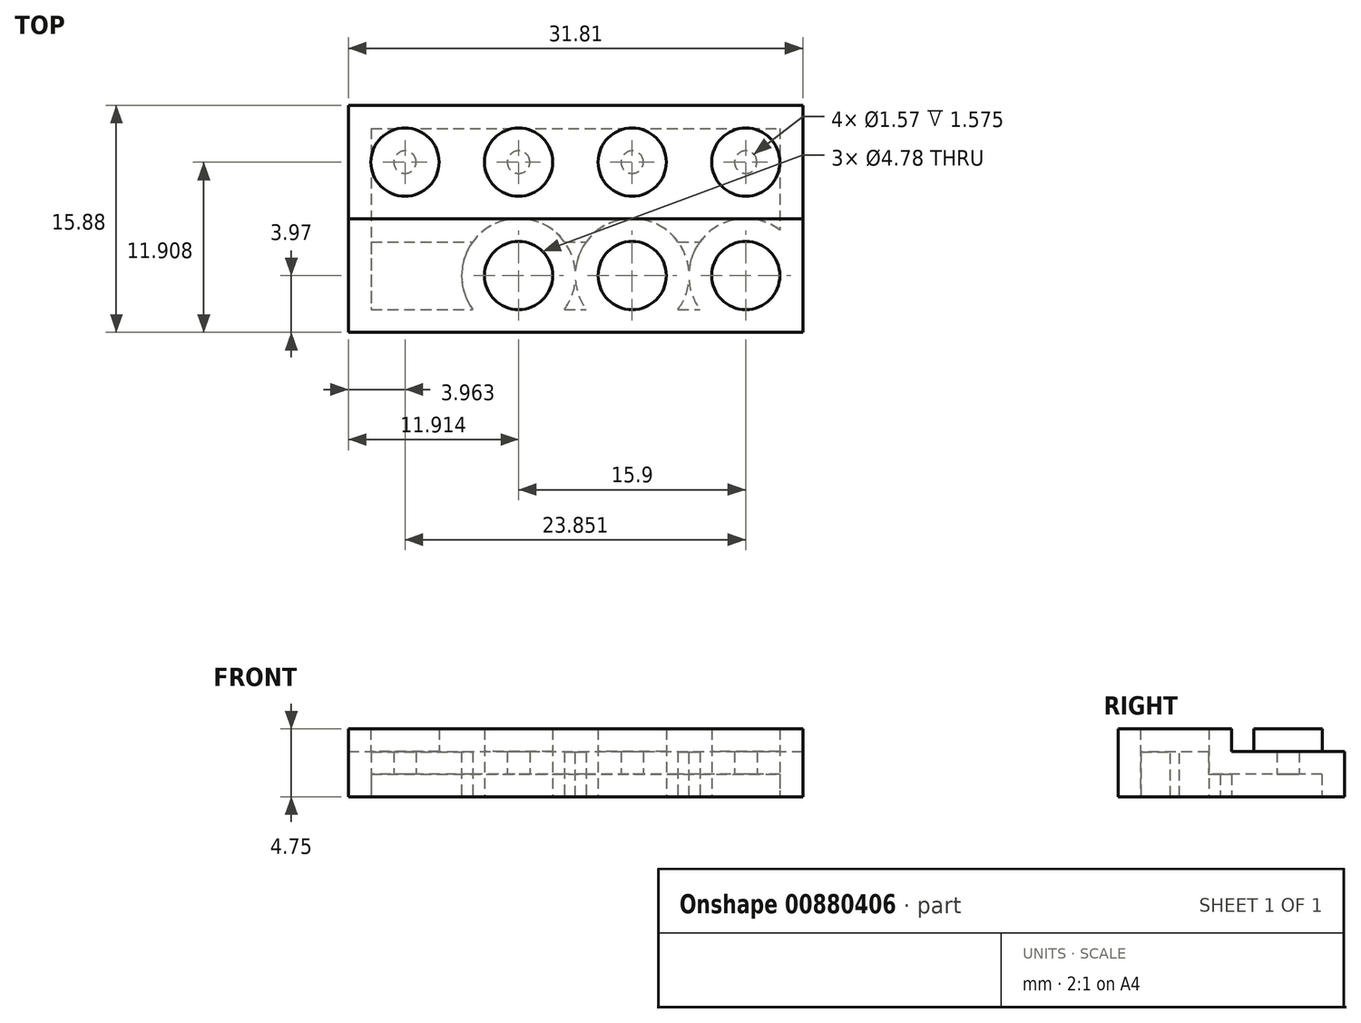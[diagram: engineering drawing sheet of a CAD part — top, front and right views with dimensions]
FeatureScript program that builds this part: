
annotation { "Feature Type Name" : "Feature", "Feature Type Description" : "" }
export const myFeature = defineFeature(function(context is Context, id is Id, definition is map)
    precondition{}
    {
        {
            var Q0;
            Q0=qCreatedBy(makeId("Top.planeOp"),FACE);
            var sketch = newSketch(context, id + "F0", { "sketchPlane" : qUnion([Q0])});
            skLineSegment(sketch, "E0.bottom", {"start": v(-38.8, 8.6) * mm, "end": v(-7, 8.6) * mm});
            skLineSegment(sketch, "E0.top", {"start": v(-38.8, -7.28) * mm, "end": v(-7, -7.28) * mm});
            skLineSegment(sketch, "E0.left", {"start": v(-38.8, 8.6) * mm, "end": v(-38.8, -7.28) * mm});
            skLineSegment(sketch, "E0.right", {"start": v(-7, 8.6) * mm, "end": v(-7, -7.28) * mm});
            skLineSegment(sketch, "E1", {"start": v(-38.8, 0.66) * mm, "end": v(-7, 0.66) * mm});
            skLineSegment(sketch, "E2", {"start": v(-7, 8.6) * mm, "end": v(-7, 0.66) * mm});
            skLineSegment(sketch, "E3", {"start": v(-7, 0.66) * mm, "end": v(-7, -7.28) * mm});
            skLineSegment(sketch, "E4", {"start": v(-38.8, 8.6) * mm, "end": v(-38.8, 0.66) * mm});
            skLineSegment(sketch, "E5", {"start": v(-38.8, -7.28) * mm, "end": v(-38.8, 0.66) * mm});
            skLineSegment(sketch, "E6", {"start": v(-7, -3.31) * mm, "end": v(-38.8, -3.31) * mm});
            skLineSegment(sketch, "E7", {"start": v(-38.8, -3.31) * mm, "end": v(-38.8, 4.63) * mm});
            skLineSegment(sketch, "E8", {"start": v(-38.8, 4.63) * mm, "end": v(-7, 4.63) * mm});
            skCircle(sketch, "E9", {"center": v(-34.85, 4.63) * mm, "radius": 2.39 * mm});
            skCircle(sketch, "E10.1.0.0", {"center": v(-26.9, 4.63) * mm, "radius": 2.39 * mm});
            skCircle(sketch, "E10.2.0.0", {"center": v(-18.95, 4.63) * mm, "radius": 2.39 * mm});
            skCircle(sketch, "E10.3.0.0", {"center": v(-11, 4.63) * mm, "radius": 2.39 * mm});
            skLineSegment(sketch, "E10.direction1", {"start": v(-34.85, 4.63) * mm, "end": v(-26.9, 4.63) * mm, "construction": true});
            skCircle(sketch, "E11.MirrorC", {"center": v(-34.85, -3.31) * mm, "radius": 2.39 * mm});
            skCircle(sketch, "E12.MirrorC", {"center": v(-26.9, -3.31) * mm, "radius": 2.39 * mm});
            skCircle(sketch, "E13.MirrorC", {"center": v(-18.95, -3.31) * mm, "radius": 2.39 * mm});
            skCircle(sketch, "E14.MirrorC", {"center": v(-11, -3.31) * mm, "radius": 2.39 * mm});
            skSolve(sketch);
        }
        {
            var Q0;
            {var subQ8=sQuery(id+"F0.wireOp",EDGE,"E0.bottom");Q0=makeQuery(id+"F0.imprint","IMPRINT",FACE,{"disambiguationData":[TD([[makeQuery(id+"F0.imprint","IMPRINT",EDGE,{"derivedFrom":subQ8}),-1.0]])]});}
            var Q1;
            {var subQ12=sQuery(id+"F0.wireOp",EDGE,"E1");Q1=makeQuery(id+"F0.imprint","IMPRINT",FACE,{"disambiguationData":[TD([[makeQuery(id+"F0.imprint","IMPRINT",EDGE,{"derivedFrom":subQ12}),1.0]])]});}
            var Q2;
            {var subQ12=sQuery(id+"F0.wireOp",EDGE,"E0.top");Q2=makeQuery(id+"F0.imprint","IMPRINT",FACE,{"disambiguationData":[TD([[makeQuery(id+"F0.imprint","IMPRINT",EDGE,{"derivedFrom":subQ12}),1.0]])]});}
            var Q3;
            {var subQ8=sQuery(id+"F0.wireOp",EDGE,"E1");Q3=makeQuery(id+"F0.imprint","IMPRINT",FACE,{"disambiguationData":[TD([[makeQuery(id+"F0.imprint","IMPRINT",EDGE,{"derivedFrom":subQ8}),-1.0]])]});}
            extrude(context, id + "F1", {"entities" : qUnion([Q0, Q1, Q2, Q3]), "depth" : 3.17 * mm, "offsetDistance" : 25.4 * mm});
        }
        {
            var Q0;
            {var subQ0=sQuery(id+"F0.wireOp",EDGE,"E9");var subQ1=sQuery(id+"F0.wireOp",EDGE,"E8");var subQ2=makeQuery(id+"F0.imprint","INTERSECT",VERTEX,{"disambiguationData":[OD(0.0)],"derivedFrom":[subQ1,subQ0]});Q0=makeQuery(id+"F0.imprint","IMPRINT",FACE,{"disambiguationData":[TD([[makeQuery(id+"F0.imprint","IMPRINT",EDGE,{"disambiguationData":[TD([[subQ2,-1.0]])],"derivedFrom":subQ1}),-1.0]])]});}
            var Q1;
            {var subQ0=sQuery(id+"F0.wireOp",EDGE,"E9");var subQ1=sQuery(id+"F0.wireOp",EDGE,"E8");var subQ2=makeQuery(id+"F0.imprint","INTERSECT",VERTEX,{"disambiguationData":[OD(0.0)],"derivedFrom":[subQ1,subQ0]});Q1=makeQuery(id+"F0.imprint","IMPRINT",FACE,{"disambiguationData":[TD([[makeQuery(id+"F0.imprint","IMPRINT",EDGE,{"disambiguationData":[TD([[subQ2,-1.0]])],"derivedFrom":subQ1}),1.0]])]});}
            var Q2;
            {var subQ0=sQuery(id+"F0.wireOp",EDGE,"E11.MirrorC");var subQ1=sQuery(id+"F0.wireOp",EDGE,"E6");var subQ2=makeQuery(id+"F0.imprint","INTERSECT",VERTEX,{"disambiguationData":[OD(0.0)],"derivedFrom":[subQ1,subQ0]});Q2=makeQuery(id+"F0.imprint","IMPRINT",FACE,{"disambiguationData":[TD([[makeQuery(id+"F0.imprint","IMPRINT",EDGE,{"disambiguationData":[TD([[subQ2,-1.0]])],"derivedFrom":subQ1}),-1.0]])]});}
            var Q3;
            {var subQ0=sQuery(id+"F0.wireOp",EDGE,"E11.MirrorC");var subQ1=sQuery(id+"F0.wireOp",EDGE,"E6");var subQ2=makeQuery(id+"F0.imprint","INTERSECT",VERTEX,{"disambiguationData":[OD(0.0)],"derivedFrom":[subQ1,subQ0]});Q3=makeQuery(id+"F0.imprint","IMPRINT",FACE,{"disambiguationData":[TD([[makeQuery(id+"F0.imprint","IMPRINT",EDGE,{"disambiguationData":[TD([[subQ2,-1.0]])],"derivedFrom":subQ1}),1.0]])]});}
            var Q4;
            {var subQ0=sQuery(id+"F0.wireOp",EDGE,"E12.MirrorC");var subQ1=sQuery(id+"F0.wireOp",EDGE,"E6");var subQ2=makeQuery(id+"F0.imprint","INTERSECT",VERTEX,{"disambiguationData":[OD(0.0)],"derivedFrom":[subQ1,subQ0]});Q4=makeQuery(id+"F0.imprint","IMPRINT",FACE,{"disambiguationData":[TD([[makeQuery(id+"F0.imprint","IMPRINT",EDGE,{"disambiguationData":[TD([[subQ2,-1.0]])],"derivedFrom":subQ1}),1.0]])]});}
            var Q5;
            {var subQ0=sQuery(id+"F0.wireOp",EDGE,"E12.MirrorC");var subQ1=sQuery(id+"F0.wireOp",EDGE,"E6");var subQ2=makeQuery(id+"F0.imprint","INTERSECT",VERTEX,{"disambiguationData":[OD(0.0)],"derivedFrom":[subQ1,subQ0]});Q5=makeQuery(id+"F0.imprint","IMPRINT",FACE,{"disambiguationData":[TD([[makeQuery(id+"F0.imprint","IMPRINT",EDGE,{"disambiguationData":[TD([[subQ2,-1.0]])],"derivedFrom":subQ1}),-1.0]])]});}
            var Q6;
            {var subQ0=sQuery(id+"F0.wireOp",EDGE,"E10.1.0.0");var subQ1=sQuery(id+"F0.wireOp",EDGE,"E8");var subQ2=makeQuery(id+"F0.imprint","INTERSECT",VERTEX,{"disambiguationData":[OD(0.0)],"derivedFrom":[subQ1,subQ0]});Q6=makeQuery(id+"F0.imprint","IMPRINT",FACE,{"disambiguationData":[TD([[makeQuery(id+"F0.imprint","IMPRINT",EDGE,{"disambiguationData":[TD([[subQ2,-1.0]])],"derivedFrom":subQ1}),-1.0]])]});}
            var Q7;
            {var subQ0=sQuery(id+"F0.wireOp",EDGE,"E10.1.0.0");var subQ1=sQuery(id+"F0.wireOp",EDGE,"E8");var subQ2=makeQuery(id+"F0.imprint","INTERSECT",VERTEX,{"disambiguationData":[OD(0.0)],"derivedFrom":[subQ1,subQ0]});Q7=makeQuery(id+"F0.imprint","IMPRINT",FACE,{"disambiguationData":[TD([[makeQuery(id+"F0.imprint","IMPRINT",EDGE,{"disambiguationData":[TD([[subQ2,-1.0]])],"derivedFrom":subQ1}),1.0]])]});}
            var Q8;
            {var subQ0=sQuery(id+"F0.wireOp",EDGE,"E13.MirrorC");var subQ1=sQuery(id+"F0.wireOp",EDGE,"E6");var subQ2=makeQuery(id+"F0.imprint","INTERSECT",VERTEX,{"disambiguationData":[OD(0.0)],"derivedFrom":[subQ1,subQ0]});Q8=makeQuery(id+"F0.imprint","IMPRINT",FACE,{"disambiguationData":[TD([[makeQuery(id+"F0.imprint","IMPRINT",EDGE,{"disambiguationData":[TD([[subQ2,-1.0]])],"derivedFrom":subQ1}),1.0]])]});}
            var Q9;
            {var subQ0=sQuery(id+"F0.wireOp",EDGE,"E13.MirrorC");var subQ1=sQuery(id+"F0.wireOp",EDGE,"E6");var subQ2=makeQuery(id+"F0.imprint","INTERSECT",VERTEX,{"disambiguationData":[OD(0.0)],"derivedFrom":[subQ1,subQ0]});Q9=makeQuery(id+"F0.imprint","IMPRINT",FACE,{"disambiguationData":[TD([[makeQuery(id+"F0.imprint","IMPRINT",EDGE,{"disambiguationData":[TD([[subQ2,-1.0]])],"derivedFrom":subQ1}),-1.0]])]});}
            var Q10;
            {var subQ0=sQuery(id+"F0.wireOp",EDGE,"E10.2.0.0");var subQ1=sQuery(id+"F0.wireOp",EDGE,"E8");var subQ2=makeQuery(id+"F0.imprint","INTERSECT",VERTEX,{"disambiguationData":[OD(0.0)],"derivedFrom":[subQ1,subQ0]});Q10=makeQuery(id+"F0.imprint","IMPRINT",FACE,{"disambiguationData":[TD([[makeQuery(id+"F0.imprint","IMPRINT",EDGE,{"disambiguationData":[TD([[subQ2,-1.0]])],"derivedFrom":subQ1}),1.0]])]});}
            var Q11;
            {var subQ0=sQuery(id+"F0.wireOp",EDGE,"E10.2.0.0");var subQ1=sQuery(id+"F0.wireOp",EDGE,"E8");var subQ2=makeQuery(id+"F0.imprint","INTERSECT",VERTEX,{"disambiguationData":[OD(0.0)],"derivedFrom":[subQ1,subQ0]});Q11=makeQuery(id+"F0.imprint","IMPRINT",FACE,{"disambiguationData":[TD([[makeQuery(id+"F0.imprint","IMPRINT",EDGE,{"disambiguationData":[TD([[subQ2,-1.0]])],"derivedFrom":subQ1}),-1.0]])]});}
            var Q12;
            {var subQ0=sQuery(id+"F0.wireOp",EDGE,"E14.MirrorC");var subQ1=sQuery(id+"F0.wireOp",EDGE,"E6");var subQ2=makeQuery(id+"F0.imprint","INTERSECT",VERTEX,{"disambiguationData":[OD(0.0)],"derivedFrom":[subQ1,subQ0]});Q12=makeQuery(id+"F0.imprint","IMPRINT",FACE,{"disambiguationData":[TD([[makeQuery(id+"F0.imprint","IMPRINT",EDGE,{"disambiguationData":[TD([[subQ2,-1.0]])],"derivedFrom":subQ1}),-1.0]])]});}
            var Q13;
            {var subQ0=sQuery(id+"F0.wireOp",EDGE,"E14.MirrorC");var subQ1=sQuery(id+"F0.wireOp",EDGE,"E6");var subQ2=makeQuery(id+"F0.imprint","INTERSECT",VERTEX,{"disambiguationData":[OD(0.0)],"derivedFrom":[subQ1,subQ0]});Q13=makeQuery(id+"F0.imprint","IMPRINT",FACE,{"disambiguationData":[TD([[makeQuery(id+"F0.imprint","IMPRINT",EDGE,{"disambiguationData":[TD([[subQ2,-1.0]])],"derivedFrom":subQ1}),1.0]])]});}
            var Q14;
            {var subQ0=sQuery(id+"F0.wireOp",EDGE,"E10.3.0.0");var subQ1=sQuery(id+"F0.wireOp",EDGE,"E8");var subQ2=makeQuery(id+"F0.imprint","INTERSECT",VERTEX,{"disambiguationData":[OD(0.0)],"derivedFrom":[subQ1,subQ0]});Q14=makeQuery(id+"F0.imprint","IMPRINT",FACE,{"disambiguationData":[TD([[makeQuery(id+"F0.imprint","IMPRINT",EDGE,{"disambiguationData":[TD([[subQ2,-1.0]])],"derivedFrom":subQ1}),-1.0]])]});}
            var Q15;
            {var subQ0=sQuery(id+"F0.wireOp",EDGE,"E10.3.0.0");var subQ1=sQuery(id+"F0.wireOp",EDGE,"E8");var subQ2=makeQuery(id+"F0.imprint","INTERSECT",VERTEX,{"disambiguationData":[OD(0.0)],"derivedFrom":[subQ1,subQ0]});Q15=makeQuery(id+"F0.imprint","IMPRINT",FACE,{"disambiguationData":[TD([[makeQuery(id+"F0.imprint","IMPRINT",EDGE,{"disambiguationData":[TD([[subQ2,-1.0]])],"derivedFrom":subQ1}),1.0]])]});}
            extrude(context, id + "F2", {"entities" : qUnion([Q0, Q1, Q2, Q3, Q4, Q5, Q6, Q7, Q8, Q9, Q10, Q11, Q12, Q13, Q14, Q15]), "operationType" : NewBodyOperationType.ADD, "depth" : 4.75 * mm, "offsetDistance" : 25.4 * mm});
        }
        {
            var Q0;
            {var subQ0=sQuery(id+"F0.wireOp",EDGE,"E14.MirrorC");var subQ1=sQuery(id+"F0.wireOp",EDGE,"E13.MirrorC");var subQ2=sQuery(id+"F0.wireOp",EDGE,"E12.MirrorC");var subQ3=sQuery(id+"F0.wireOp",EDGE,"E11.MirrorC");var subQ4=sQuery(id+"F0.wireOp",EDGE,"E10.3.0.0");var subQ5=sQuery(id+"F0.wireOp",EDGE,"E10.2.0.0");var subQ6=sQuery(id+"F0.wireOp",EDGE,"E10.1.0.0");var subQ7=sQuery(id+"F0.wireOp",EDGE,"E9");Q0=makeQuery(id+"F2.boolean.opBoolean","MERGE",FACE,{"derivedFrom":[makeQuery(id+"F1.opExtrude","CAP_FACE",FACE,{"disambiguationData":[OSD([sQuery(id+"F0.wireOp",EDGE,"E0.bottom"),sQuery(id+"F0.wireOp",EDGE,"E0.top"),sQuery(id+"F0.wireOp",EDGE,"E2"),sQuery(id+"F0.wireOp",EDGE,"E3"),sQuery(id+"F0.wireOp",EDGE,"E4"),sQuery(id+"F0.wireOp",EDGE,"E5"),sQuery(id+"F0.wireOp",EDGE,"E7"),subQ7,subQ6,subQ5,subQ4,subQ3,subQ2,subQ1,subQ0])],"isStart":true}),makeQuery(id+"F2.opExtrude","CAP_FACE",FACE,{"disambiguationData":[OSD([subQ7])],"isStart":true}),makeQuery(id+"F2.opExtrude","CAP_FACE",FACE,{"disambiguationData":[OSD([subQ6])],"isStart":true}),makeQuery(id+"F2.opExtrude","CAP_FACE",FACE,{"disambiguationData":[OSD([subQ5])],"isStart":true}),makeQuery(id+"F2.opExtrude","CAP_FACE",FACE,{"disambiguationData":[OSD([subQ4])],"isStart":true}),makeQuery(id+"F2.opExtrude","CAP_FACE",FACE,{"disambiguationData":[OSD([subQ3])],"isStart":true}),makeQuery(id+"F2.opExtrude","CAP_FACE",FACE,{"disambiguationData":[OSD([subQ2])],"isStart":true}),makeQuery(id+"F2.opExtrude","CAP_FACE",FACE,{"disambiguationData":[OSD([subQ1])],"isStart":true}),makeQuery(id+"F2.opExtrude","CAP_FACE",FACE,{"disambiguationData":[OSD([subQ0])],"isStart":true})]});}
            shell(context, id + "F3", {"entities" : qUnion([Q0]), "thickness" : 1.6 * mm});
        }
    });
